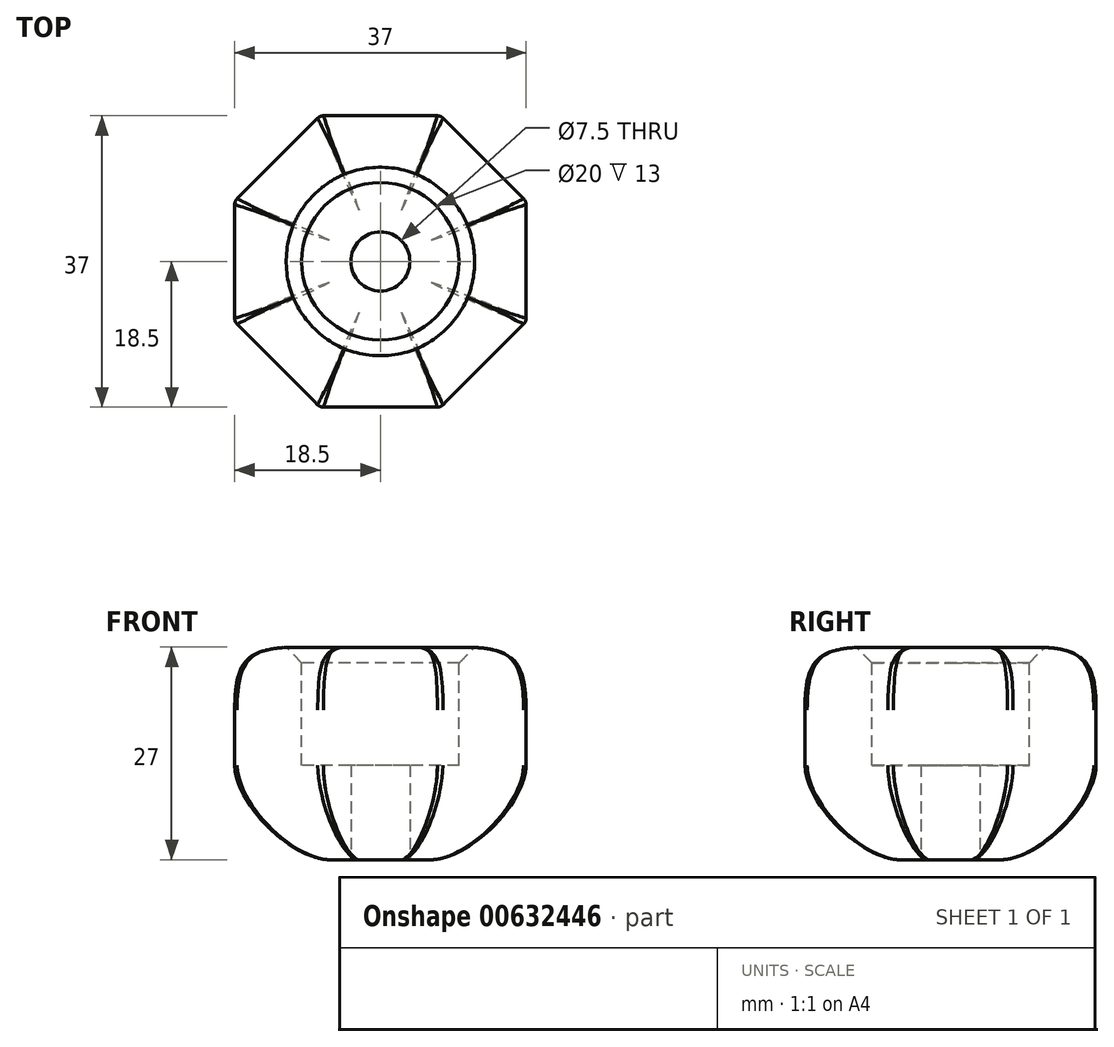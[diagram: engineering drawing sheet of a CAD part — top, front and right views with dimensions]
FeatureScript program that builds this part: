
annotation { "Feature Type Name" : "Feature", "Feature Type Description" : "" }
export const myFeature = defineFeature(function(context is Context, id is Id, definition is map)
    precondition{}
    {
        {
            var Q0;
            Q0=qCreatedBy(makeId("Top.planeOp"),FACE);
            var sketch = newSketch(context, id + "F0", { "sketchPlane" : qUnion([Q0])});
            skCircle(sketch, "E0.cCircle", {"center": v(0, 0) * mm, "radius": 18.5 * mm, "construction": true});
            skLineSegment(sketch, "E0.0", {"start": v(-7.66, 18.5) * mm, "end": v(7.66, 18.5) * mm});
            skLineSegment(sketch, "E0.1", {"start": v(7.66, 18.5) * mm, "end": v(18.5, 7.66) * mm});
            skLineSegment(sketch, "E0.2", {"start": v(18.5, 7.66) * mm, "end": v(18.5, -7.66) * mm});
            skLineSegment(sketch, "E0.3", {"start": v(18.5, -7.66) * mm, "end": v(7.66, -18.5) * mm});
            skLineSegment(sketch, "E0.4", {"start": v(7.66, -18.5) * mm, "end": v(-7.66, -18.5) * mm});
            skLineSegment(sketch, "E0.5", {"start": v(-7.66, -18.5) * mm, "end": v(-18.5, -7.66) * mm});
            skLineSegment(sketch, "E0.6", {"start": v(-18.5, -7.66) * mm, "end": v(-18.5, 7.66) * mm});
            skLineSegment(sketch, "E0.7", {"start": v(-18.5, 7.66) * mm, "end": v(-7.66, 18.5) * mm});
            skPoint(sketch, "E0.0.midPoint", {"position": v(0, 18.5) * mm});
            skCircle(sketch, "E1", {"center": v(0, 0) * mm, "radius": 3.75 * mm});
            skSolve(sketch);
        }
        {
            var Q0;
            Q0 = qSketchRegion(id + "F0", true);
            extrude(context, id + "F1", {"entities" : qUnion([Q0]), "depth" : 27 * mm, "offsetDistance" : 25 * mm});
        }
        {
            var Q0;
            Q0=makeQuery(id+"F1.opExtrude","CAP_FACE",FACE,{"disambiguationData":[OSD([sQuery(id+"F0.wireOp",EDGE,"E0.0"),sQuery(id+"F0.wireOp",EDGE,"E0.1"),sQuery(id+"F0.wireOp",EDGE,"E0.2"),sQuery(id+"F0.wireOp",EDGE,"E0.3"),sQuery(id+"F0.wireOp",EDGE,"E0.4"),sQuery(id+"F0.wireOp",EDGE,"E0.5"),sQuery(id+"F0.wireOp",EDGE,"E0.6"),sQuery(id+"F0.wireOp",EDGE,"E0.7"),sQuery(id+"F0.wireOp",EDGE,"E1")])],"isStart":false});
            var sketch = newSketch(context, id + "F2", { "sketchPlane" : qUnion([Q0])});
            skCircle(sketch, "E2", {"center": v(0, 0) * mm, "radius": 10 * mm});
            skSolve(sketch);
        }
        {
            var Q0;
            Q0 = qSketchRegion(id + "F2", true);
            extrude(context, id + "F3", {"entities" : qUnion([Q0]), "operationType" : NewBodyOperationType.REMOVE, "oppositeDirection" : true, "depth" : 15 * mm, "offsetDistance" : 25 * mm});
        }
        {
            var Q0;
            Q0=makeQuery(id+"F1.opExtrude","CAP_EDGE",EDGE,{"disambiguationData":[OSD([sQuery(id+"F0.wireOp",EDGE,"E0.0")])],"isStart":false});
            var Q1;
            Q1=makeQuery(id+"F1.opExtrude","CAP_EDGE",EDGE,{"disambiguationData":[OSD([sQuery(id+"F0.wireOp",EDGE,"E0.7")])],"isStart":false});
            var Q2;
            Q2=makeQuery(id+"F1.opExtrude","CAP_EDGE",EDGE,{"disambiguationData":[OSD([sQuery(id+"F0.wireOp",EDGE,"E0.6")])],"isStart":false});
            var Q3;
            Q3=makeQuery(id+"F1.opExtrude","CAP_EDGE",EDGE,{"disambiguationData":[OSD([sQuery(id+"F0.wireOp",EDGE,"E0.5")])],"isStart":false});
            var Q4;
            Q4=makeQuery(id+"F1.opExtrude","CAP_EDGE",EDGE,{"disambiguationData":[OSD([sQuery(id+"F0.wireOp",EDGE,"E0.4")])],"isStart":false});
            var Q5;
            Q5=makeQuery(id+"F1.opExtrude","CAP_EDGE",EDGE,{"disambiguationData":[OSD([sQuery(id+"F0.wireOp",EDGE,"E0.3")])],"isStart":false});
            var Q6;
            Q6=makeQuery(id+"F1.opExtrude","CAP_EDGE",EDGE,{"disambiguationData":[OSD([sQuery(id+"F0.wireOp",EDGE,"E0.2")])],"isStart":false});
            var Q7;
            Q7=makeQuery(id+"F1.opExtrude","CAP_EDGE",EDGE,{"disambiguationData":[OSD([sQuery(id+"F0.wireOp",EDGE,"E0.1")])],"isStart":false});
            fillet(context, id + "F4", {"entities" : qUnion([Q0, Q1, Q2, Q3, Q4, Q5, Q6, Q7]), "radius" : 8 * mm, "tangentPropagation" : true, "rho" : 0.6, "crossSection" : FilletCrossSection.CONIC, "allowEdgeOverflow" : false});
        }
        {
            var Q0;
            Q0=makeQuery(id+"F1.opExtrude","CAP_EDGE",EDGE,{"disambiguationData":[OSD([sQuery(id+"F0.wireOp",EDGE,"E0.1")])],"isStart":true});
            var Q1;
            Q1=makeQuery(id+"F1.opExtrude","CAP_EDGE",EDGE,{"disambiguationData":[OSD([sQuery(id+"F0.wireOp",EDGE,"E0.3")])],"isStart":true});
            var Q2;
            Q2=makeQuery(id+"F1.opExtrude","CAP_EDGE",EDGE,{"disambiguationData":[OSD([sQuery(id+"F0.wireOp",EDGE,"E0.5")])],"isStart":true});
            var Q3;
            Q3=makeQuery(id+"F1.opExtrude","CAP_EDGE",EDGE,{"disambiguationData":[OSD([sQuery(id+"F0.wireOp",EDGE,"E0.7")])],"isStart":true});
            var Q4;
            Q4=makeQuery(id+"F1.opExtrude","CAP_EDGE",EDGE,{"disambiguationData":[OSD([sQuery(id+"F0.wireOp",EDGE,"E0.2")])],"isStart":true});
            var Q5;
            Q5=makeQuery(id+"F1.opExtrude","CAP_EDGE",EDGE,{"disambiguationData":[OSD([sQuery(id+"F0.wireOp",EDGE,"E0.0")])],"isStart":true});
            var Q6;
            Q6=makeQuery(id+"F1.opExtrude","CAP_EDGE",EDGE,{"disambiguationData":[OSD([sQuery(id+"F0.wireOp",EDGE,"E0.6")])],"isStart":true});
            var Q7;
            Q7=makeQuery(id+"F1.opExtrude","CAP_EDGE",EDGE,{"disambiguationData":[OSD([sQuery(id+"F0.wireOp",EDGE,"E0.4")])],"isStart":true});
            fillet(context, id + "F5", {"entities" : qUnion([Q0, Q1, Q2, Q3, Q4, Q5, Q6, Q7]), "radius" : 12 * mm, "tangentPropagation" : true, "rho" : 0.3, "crossSection" : FilletCrossSection.CONIC, "allowEdgeOverflow" : false});
        }
        {
            var Q0;
            Q0=makeQuery(id+"F1.opExtrude","CAP_FACE",FACE,{"disambiguationData":[OSD([sQuery(id+"F0.wireOp",EDGE,"E0.0"),sQuery(id+"F0.wireOp",EDGE,"E0.1"),sQuery(id+"F0.wireOp",EDGE,"E0.2"),sQuery(id+"F0.wireOp",EDGE,"E0.3"),sQuery(id+"F0.wireOp",EDGE,"E0.4"),sQuery(id+"F0.wireOp",EDGE,"E0.5"),sQuery(id+"F0.wireOp",EDGE,"E0.6"),sQuery(id+"F0.wireOp",EDGE,"E0.7"),sQuery(id+"F0.wireOp",EDGE,"E1")])],"isStart":false});
            chamfer(context, id + "F6", {"entities" : qUnion([Q0]), "width" : 2 * mm, "tangentPropagation" : true});
        }
        {
            var Q0;
            Q0=makeQuery(id+"F1.opExtrude","SWEPT_FACE",FACE,{"disambiguationData":[OSD([sQuery(id+"F0.wireOp",EDGE,"E0.0")])]});
            var Q1;
            Q1=makeQuery(id+"F1.opExtrude","SWEPT_FACE",FACE,{"disambiguationData":[OSD([sQuery(id+"F0.wireOp",EDGE,"E0.6")])]});
            var Q2;
            Q2=makeQuery(id+"F1.opExtrude","SWEPT_FACE",FACE,{"disambiguationData":[OSD([sQuery(id+"F0.wireOp",EDGE,"E0.4")])]});
            var Q3;
            Q3=makeQuery(id+"F1.opExtrude","SWEPT_FACE",FACE,{"disambiguationData":[OSD([sQuery(id+"F0.wireOp",EDGE,"E0.2")])]});
            fillet(context, id + "F7", {"entities" : qUnion([Q0, Q1, Q2, Q3]), "radius" : 1 * mm, "tangentPropagation" : true, "allowEdgeOverflow" : false});
        }
    });
